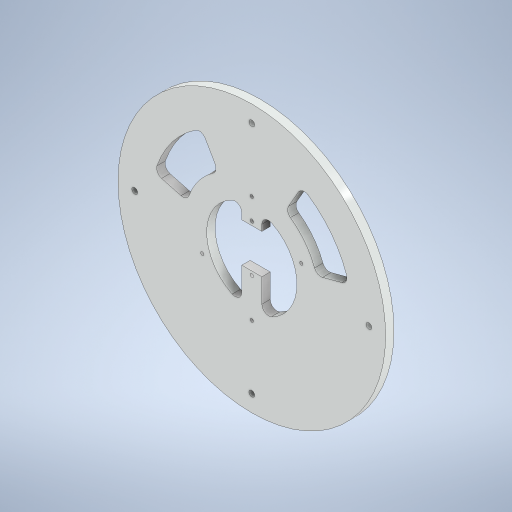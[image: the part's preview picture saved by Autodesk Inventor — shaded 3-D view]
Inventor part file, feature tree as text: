
AUTODESK INVENTOR PART (.ipt)
format: ipt  version: 2023.1 (Build 271208000, 208)  size: 334,336 bytes
history: native  units: mm
features: extrude x5, sketch x4, fillet x2, other x1, pattern_circular x1, mirror x1
ambient origin geometry x8: Origin, YZ Plane, XZ Plane, XY Plane, X Axis, Y Axis, Z Axis, Center Point
bodies: Body1 (feature_tree)
feature tree (14):
  other  "솔리드1"
  sketch  "스케치1"
  extrude  "돌출1"  Depth=160.0mm
  extrude  "돌출2"  Depth=68.0mm
  fillet  "모깎기1"  Radius=54.0mm
  extrude  "돌출3"  Depth=120.0mm
  pattern_circular  "원형 패턴2"  Count=8  [1 undecoded]
  extrude  "돌출4"  TaperAngle=45.0deg  [1 undecoded]
  fillet  "모깎기2"  Radius=5.0mm
  extrude  "돌출5"  Depth=5.0mm TaperAngle=0.0deg
  mirror  "미러1"
  sketch  "스케치2"
  sketch  "스케치3"
  sketch  "스케치4"
note: 2 required parameter values undecoded (feature->parameter linkage not recoverable at this tier; creation-order binding heuristic only, values carry confidence <= 0.55)
